# Revit family: Valve_Trim-DXV-Modulus-D35120700_Series
name_source: partatom
category: Plumbing Fixtures
revit_build: Autodesk Revit 2018 (Build: 20170223_1515(x64)
units: mm (PartAtom-declared; Revit-internal decimal feet)

## family parameters
Cut with Voids When Loaded = No
Host = Face
OmniClass Number = 23.45.05.14.17
OmniClass Title = Showers
Part Type = Normal
Room Calculation Point = No
Round Connector Dimension = Use Diameter
Shared = Yes

## types (4) — shared parameters
1/2" Wall Rough Valve D35000710.191 = Yes
3/4" Wall Rough Valve D35000700.191 = No
ADA Compliant = Yes
Assembly Code = D2010710
CW Connection = Yes
CWFU = 3
Cold Water Connection Description = 1/2'' CW NPT Inlet Connection
Cold Water Connection Diameter = 1/2"
Connection Description = 1/2'' NPT Outlet Connection
Default Elevation = 48"
Description = DXV Modulus 1/2'' Wall Valve Trim
Diameter = 3 1/16"
HW Connection = Yes
HWFU = 3
Height = 3 11/16"
Hot Water Connection Description = 1/2'' HW NPT Inlet Connection
Hot Water Connection Diameter = 1/2"
IAPMO Compliance = Meets or Exceeds ASME A112.18.1/CSA B125.1
Inlet / Outlet Depth = 1 5/8"
Inlet / Outlet Depth Constraint = 1 5/8"
Installation Type = Wall Mounted
Manufacturer = DXV
Price = Prices may vary. Please consult Manufacturer Representative for most up-to-date price list.
Product Documentation Link = https://dxv01.blob.core.windows.net
Product Page URL = https://www.dxv.com
Revised Date = 04/07/2022
URL = https://www.dxv.com
Vent Connection = No
WFU = 4
Waste Connection = No
Water Connection Diameter = 1/2"

## per-type parameters (varying)
| type | Finish | Material |
| D35120700.100 | Cast Brass-DXV-100-Polished Chrome | Cast Brass-DXV-100-Polished Chrome |
| D35120700.144 | Cast Brass-DXV-144-Brushed Nickel | Cast Brass-DXV-144-Brushed Nickel |
| D35120700.150 | Cast Brass-DXV-150-Platinum Nickel | Cast Brass-DXV-150-Platinum Nickel |
| D35120700.243 | Cast Brass-DXV-243-Matte Black | Cast Brass-DXV-243-Matte Black |

note: column(s) folded — value = type name in every type: Model

## geometry (parser evidence)
native form markers: Sweep x3
no freeform markers — native parametric forms only
